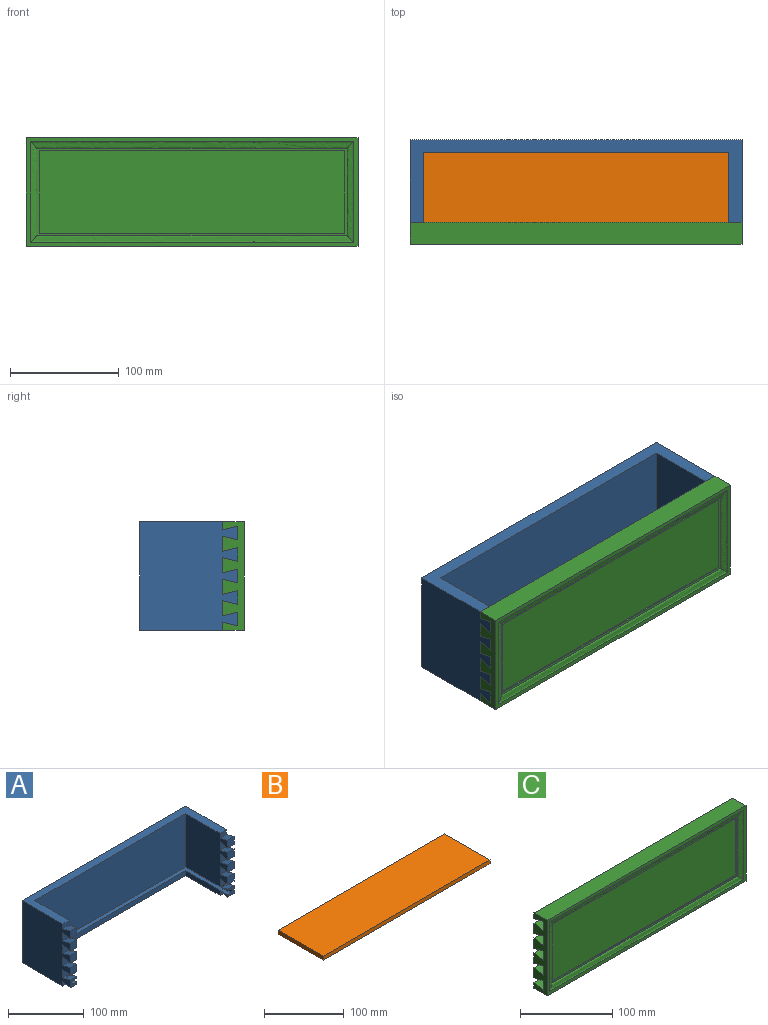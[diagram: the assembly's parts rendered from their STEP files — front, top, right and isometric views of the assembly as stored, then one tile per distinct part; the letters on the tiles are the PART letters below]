
ASSEMBLY  parts=3 mates=6
PART A: 62 faces, bbox 304.7x90x100 mm
  f0: plane 12.7x12mm, normal (0,-1,0), area 104.4mm2, adj f14,f15,f20,f25,f27,f28,f35,f48
  f1: plane 12.7x12mm, normal (0,-1,0), area 152.4mm2, adj f13,f15,f33,f44
  f2: plane 12.7x12mm, normal (0,-1,0), area 152.4mm2, adj f13,f15,f41,f46
  f3: plane 12.7x12mm, normal (0,-1,0), area 152.4mm2, adj f13,f15,f38,f43
  f4: plane 12.7x12mm, normal (0,-1,0), area 152.4mm2, adj f13,f15,f36,f40
  f5: plane 12.7x12mm, normal (0,-1,0), area 104.4mm2, adj f10,f12,f17,f18,f27,f29,f30,f60
  f6: plane 12.7x12mm, normal (0,-1,0), area 152.4mm2, adj f10,f11,f32,f59
  f7: plane 12.7x12mm, normal (0,-1,0), area 152.4mm2, adj f10,f11,f56,f57
  f8: plane 12.7x12mm, normal (0,-1,0), area 152.4mm2, adj f10,f11,f53,f54
  f9: plane 12.7x12mm, normal (0,-1,0), area 152.4mm2, adj f10,f11,f49,f51
  f10: plane 100x90mm, normal (-1,0,0), area 8244.7mm2, adj f5,f6,f7,f8,f9,f22,f23,f24
  f11: plane 86x78mm, normal (1,0,0), area 6019.7mm2, adj f6,f7,f8,f9,f16,f21,f23,f31
  f12: plane 11.68x2.91mm, normal (1,0,0), area 17mm2, adj f5,f17,f30
  f13: plane 86x78mm, normal (-1,0,0), area 6019.7mm2, adj f1,f2,f3,f4,f16,f21,f23,f33
  f14: plane 11.68x2.91mm, normal (-1,0,0), area 17mm2, adj f0,f28,f35
  f15: plane 100x90mm, normal (1,0,0), area 8244.7mm2, adj f0,f1,f2,f3,f4,f22,f23,f24
  f16: plane 296.67x72mm, normal (0,0,-1), area 3397.3mm2, adj f11,f13,f21,f25,f26,f29,f31,f34
  f17: plane 11.68x8mm, normal (0,0,-1), area 93.4mm2, adj f5,f12,f29,f30
  f18: plane 78x8mm, normal (1,0,0), area 540.6mm2, adj f5,f19,f24,f27,f60,f61
  f19: plane 280.67x8mm, normal (0,-1,0), area 2245.3mm2, adj f18,f20,f24,f27
  f20: plane 78x8mm, normal (-1,0,0), area 540.6mm2, adj f0,f19,f24,f27,f47,f48
  f21: plane 280.67x86mm, normal (0,-1,0), area 24137.3mm2, adj f11,f13,f16,f23
  f22: plane 304.67x100mm, normal (0,1,0), area 30466.7mm2, adj f10,f15,f23,f24
  f23: plane 304.67x76mm, normal (0,0,1), area 5192mm2, adj f10,f11,f13,f15,f21,f22,f37,f50
  f24: plane 304.67x76mm, normal (0,0,-1), area 5192mm2, adj f10,f15,f18,f19,f20,f22,f47,f61
  f25: plane 86x6mm, normal (-1,0,0), area 515.3mm2, adj f0,f16,f26,f27,f28,f34,f35
  f26: plane 296.67x6mm, normal (0,-1,0), area 1780mm2, adj f16,f25,f27,f29
  f27: plane 296.67x86mm, normal (0,0,1), area 3621.3mm2, adj f0,f5,f18,f19,f20,f25,f26,f29
  f28: plane 11.68x8mm, normal (0,0,-1), area 93.4mm2, adj f0,f14,f25,f35
  f29: plane 86x6mm, normal (1,0,0), area 515.3mm2, adj f5,f16,f17,f26,f27,f30,f31
  f30: plane 14x12mm, normal (0,0.24,0.97), area 154mm2, adj f5,f10,f12,f17,f29,f31
  f31: plane 14x12mm, normal (0,-1,0), area 163.4mm2, adj f10,f11,f16,f29,f30,f32
  f32: plane 14x12mm, normal (0,0.24,-0.97), area 173.1mm2, adj f6,f10,f11,f31
  f33: plane 14x12mm, normal (0,0.24,-0.97), area 173.1mm2, adj f1,f13,f15,f34
  f34: plane 14x12mm, normal (0,-1,0), area 163.4mm2, adj f13,f15,f16,f25,f33,f35
  f35: plane 14x12mm, normal (0,0.24,0.97), area 154mm2, adj f0,f14,f15,f25,f28,f34
  f36: plane 14x12mm, normal (0,0.24,0.97), area 173.1mm2, adj f4,f13,f15,f37
  f37: plane 12x7.7mm, normal (0,-1,0), area 92.4mm2, adj f13,f15,f23,f36
  f38: plane 14x12mm, normal (0,0.24,0.97), area 173.1mm2, adj f3,f13,f15,f39
  f39: plane 14x12mm, normal (0,-1,0), area 168mm2, adj f13,f15,f38,f40
  f40: plane 14x12mm, normal (0,0.24,-0.97), area 173.1mm2, adj f4,f13,f15,f39
  f41: plane 14x12mm, normal (0,0.24,0.97), area 173.1mm2, adj f2,f13,f15,f42
  f42: plane 14x12mm, normal (0,-1,0), area 168mm2, adj f13,f15,f41,f43
  f43: plane 14x12mm, normal (0,0.24,-0.97), area 173.1mm2, adj f3,f13,f15,f42
  f44: plane 14x12mm, normal (0,0.24,0.97), area 173.1mm2, adj f1,f13,f15,f45
  f45: plane 14x12mm, normal (0,-1,0), area 168mm2, adj f13,f15,f44,f46
  f46: plane 14x12mm, normal (0,0.24,-0.97), area 173.1mm2, adj f2,f13,f15,f45
  f47: plane 12x7.7mm, normal (0,-1,0), area 92.4mm2, adj f15,f20,f24,f48
  f48: plane 14x12mm, normal (0,0.24,-0.97), area 173.1mm2, adj f0,f15,f20,f47
  f49: plane 14x12mm, normal (0,0.24,0.97), area 173.1mm2, adj f9,f10,f11,f50
  f50: plane 12x7.7mm, normal (0,-1,0), area 92.4mm2, adj f10,f11,f23,f49
  f51: plane 14x12mm, normal (0,0.24,-0.97), area 173.1mm2, adj f9,f10,f11,f52
  f52: plane 14x12mm, normal (0,-1,0), area 168mm2, adj f10,f11,f51,f53
  f53: plane 14x12mm, normal (0,0.24,0.97), area 173.1mm2, adj f8,f10,f11,f52
  f54: plane 14x12mm, normal (0,0.24,-0.97), area 173.1mm2, adj f8,f10,f11,f55
  f55: plane 14x12mm, normal (0,-1,0), area 168mm2, adj f10,f11,f54,f56
  f56: plane 14x12mm, normal (0,0.24,0.97), area 173.1mm2, adj f7,f10,f11,f55
  f57: plane 14x12mm, normal (0,0.24,-0.97), area 173.1mm2, adj f7,f10,f11,f58
  f58: plane 14x12mm, normal (0,-1,0), area 168mm2, adj f10,f11,f57,f59
  f59: plane 14x12mm, normal (0,0.24,0.97), area 173.1mm2, adj f6,f10,f11,f58
  f60: plane 14x12mm, normal (0,0.24,-0.97), area 173.1mm2, adj f5,f10,f18,f61
  f61: plane 12x7.7mm, normal (0,-1,0), area 92.4mm2, adj f10,f18,f24,f60
PART B: 6 faces, bbox 296.7x80x6 mm
  f0: plane 80x6mm, normal (-1,0,0), area 480mm2, adj f1,f3,f4,f5
  f1: plane 296.67x6mm, normal (0,-1,0), area 1780mm2, adj f0,f2,f4,f5
  f2: plane 80x6mm, normal (1,0,0), area 480mm2, adj f1,f3,f4,f5
  f3: plane 296.67x6mm, normal (0,1,0), area 1780mm2, adj f0,f2,f4,f5
  f4: plane 296.67x80mm, normal (0,0,1), area 23733.3mm2, adj f0,f1,f2,f3
  f5: plane 296.67x80mm, normal (0,0,-1), area 23733.3mm2, adj f0,f1,f2,f3
PART C: 60 faces, bbox 304.7x20x100 mm
  f0: plane 304.67x8mm, normal (0,1,0), area 2430.2mm2, adj f2,f4,f5,f8,f10,f27,f29,f57
  f1: plane 12x11.68mm, normal (0,-0.24,-0.97), area 144.5mm2, adj f4,f9,f10,f58
  f2: plane 100x20mm, normal (1,0,0), area 1354.7mm2, adj f0,f3,f5,f6,f7,f27,f28,f30
  f3: plane 12x11.68mm, normal (0,-0.24,-0.97), area 144.5mm2, adj f2,f28,f29,f58
  f4: plane 100x20mm, normal (-1,0,0), area 1354.7mm2, adj f0,f1,f5,f6,f7,f8,f9,f11
  f5: plane 304.67x20mm, normal (0,0,-1), area 6093.3mm2, adj f0,f2,f4,f54
  f6: plane 304.67x20mm, normal (0,0,1), area 6093.3mm2, adj f2,f4,f7,f54
  f7: plane 304.67x86mm, normal (0,1,0), area 25652.3mm2, adj f2,f4,f6,f11,f12,f14,f15,f16
  f8: plane 14x12mm, normal (0,-0.24,0.97), area 173.1mm2, adj f0,f4,f9,f10
  f9: plane 12.7x12mm, normal (0,1,0), area 152.4mm2, adj f1,f4,f8,f10
  f10: plane 14x12.7mm, normal (-1,0,0), area 81.6mm2, adj f0,f1,f8,f9,f57,f58,f59
  f11: plane 14x12mm, normal (0,-0.24,-0.97), area 173.1mm2, adj f4,f7,f13,f14
  f12: plane 14x12mm, normal (0,-0.24,0.97), area 173.1mm2, adj f4,f7,f13,f14
  f13: plane 12.7x12mm, normal (0,1,0), area 152.4mm2, adj f4,f11,f12,f14
  f14: plane 14x12.7mm, normal (-1,0,0), area 128.9mm2, adj f7,f11,f12,f13
  f15: plane 14x12mm, normal (0,-0.24,-0.97), area 173.1mm2, adj f4,f7,f17,f18
  f16: plane 14x12mm, normal (0,-0.24,0.97), area 173.1mm2, adj f4,f7,f17,f18
  f17: plane 12.7x12mm, normal (0,1,0), area 152.4mm2, adj f4,f15,f16,f18
  f18: plane 14x12.7mm, normal (-1,0,0), area 128.9mm2, adj f7,f15,f16,f17
  f19: plane 14x12mm, normal (0,-0.24,-0.97), area 173.1mm2, adj f4,f7,f21,f22
  f20: plane 14x12mm, normal (0,-0.24,0.97), area 173.1mm2, adj f4,f7,f21,f22
  f21: plane 12.7x12mm, normal (0,1,0), area 152.4mm2, adj f4,f19,f20,f22
  f22: plane 14x12.7mm, normal (-1,0,0), area 128.9mm2, adj f7,f19,f20,f21
  f23: plane 14x12mm, normal (0,-0.24,-0.97), area 173.1mm2, adj f4,f7,f25,f26
  f24: plane 14x12mm, normal (0,-0.24,0.97), area 173.1mm2, adj f4,f7,f25,f26
  f25: plane 12.7x12mm, normal (0,1,0), area 152.4mm2, adj f4,f23,f24,f26
  f26: plane 14x12.7mm, normal (-1,0,0), area 128.9mm2, adj f7,f23,f24,f25
  f27: plane 14x12mm, normal (0,-0.24,0.97), area 173.1mm2, adj f0,f2,f28,f29
  f28: plane 12.7x12mm, normal (0,1,0), area 152.4mm2, adj f2,f3,f27,f29
  f29: plane 14x12.7mm, normal (1,0,0), area 81.6mm2, adj f0,f3,f27,f28,f57,f58,f59
  f30: plane 14x12mm, normal (0,-0.24,-0.97), area 173.1mm2, adj f2,f7,f32,f33
  f31: plane 14x12mm, normal (0,-0.24,0.97), area 173.1mm2, adj f2,f7,f32,f33
  f32: plane 12.7x12mm, normal (0,1,0), area 152.4mm2, adj f2,f30,f31,f33
  f33: plane 14x12.7mm, normal (1,0,0), area 128.9mm2, adj f7,f30,f31,f32
  f34: plane 14x12mm, normal (0,-0.24,-0.97), area 173.1mm2, adj f2,f7,f36,f37
  f35: plane 14x12mm, normal (0,-0.24,0.97), area 173.1mm2, adj f2,f7,f36,f37
  f36: plane 12.7x12mm, normal (0,1,0), area 152.4mm2, adj f2,f34,f35,f37
  f37: plane 14x12.7mm, normal (1,0,0), area 128.9mm2, adj f7,f34,f35,f36
  f38: plane 14x12mm, normal (0,-0.24,-0.97), area 173.1mm2, adj f2,f7,f40,f41
  f39: plane 14x12mm, normal (0,-0.24,0.97), area 173.1mm2, adj f2,f7,f40,f41
  f40: plane 12.7x12mm, normal (0,1,0), area 152.4mm2, adj f2,f38,f39,f41
  f41: plane 14x12.7mm, normal (1,0,0), area 128.9mm2, adj f7,f38,f39,f40
  f42: plane 14x12mm, normal (0,-0.24,-0.97), area 173.1mm2, adj f2,f7,f44,f45
  f43: plane 14x12mm, normal (0,-0.24,0.97), area 173.1mm2, adj f2,f7,f44,f45
  f44: plane 12.7x12mm, normal (0,1,0), area 152.4mm2, adj f2,f42,f43,f45
  f45: plane 14x12.7mm, normal (1,0,0), area 128.9mm2, adj f7,f42,f43,f44
  f46: bspline ~304.67x6mm, area 2138.5mm2, adj f48,f50,f52,f54
  f47: plane 280.67x1mm, normal (0,0,1), area 280.7mm2, adj f49,f51,f52,f56
  f48: bspline ~100x6mm, area 631.9mm2, adj f46,f52,f53,f54
  f49: plane 76x1mm, normal (-1,0,0), area 76mm2, adj f47,f52,f55,f56
  f50: bspline ~100x6mm, area 631.9mm2, adj f46,f52,f53,f54
  f51: plane 76x1mm, normal (1,0,0), area 76mm2, adj f47,f52,f55,f56
  f52: plane 284.67x80mm, normal (0,-1,0), area 1442.7mm2, adj f46,f47,f48,f49,f50,f51,f53,f55
  f53: bspline ~304.67x6mm, area 2138.5mm2, adj f48,f50,f52,f54
  f54: plane 304.67x100mm, normal (0,-1,0), area 3173.3mm2, adj f2,f4,f5,f6,f46,f48,f50,f53
  f55: plane 280.67x1mm, normal (0,0,-1), area 280.7mm2, adj f49,f51,f52,f56
  f56: plane 280.67x76mm, normal (0,-1,0), area 21330.7mm2, adj f47,f49,f51,f55
  f57: plane 280.67x8mm, normal (0,0,1), area 2245.3mm2, adj f0,f10,f29,f59
  f58: plane 304.67x8mm, normal (0,0,-1), area 2301mm2, adj f1,f2,f3,f4,f7,f10,f29,f59
  f59: plane 280.67x6mm, normal (0,1,0), area 1684mm2, adj f10,f29,f57,f58
PLACE A t=(-19.43,-78.22,3.55)mm
PLACE B t=(-18.41,-178.11,11.55)mm
PLACE C t=(-19.43,-64.22,3.55)mm
MATE planar C.f4 <-> A.f10  axis (-1,0,0) through (-19.43,-64.22,99.7)mm
MATE planar B.f4 <-> C.f58  axis (0,0,1) through (132.9,-32.22,17.55)mm
MATE planar C.f6 <-> A.f23  axis (0,0,1) through (132.9,-74.22,103.55)mm
MATE planar B.f0 <-> A.f29  axis (-1,0,0) through (-15.43,-72.22,14.55)mm
MATE planar C.f59 <-> B.f1  axis (0,1,0) through (132.9,-72.22,14.55)mm
MATE planar A.f9 <-> C.f25  axis (0,-1,0) through (-13.43,-78.22,92.99)mm
